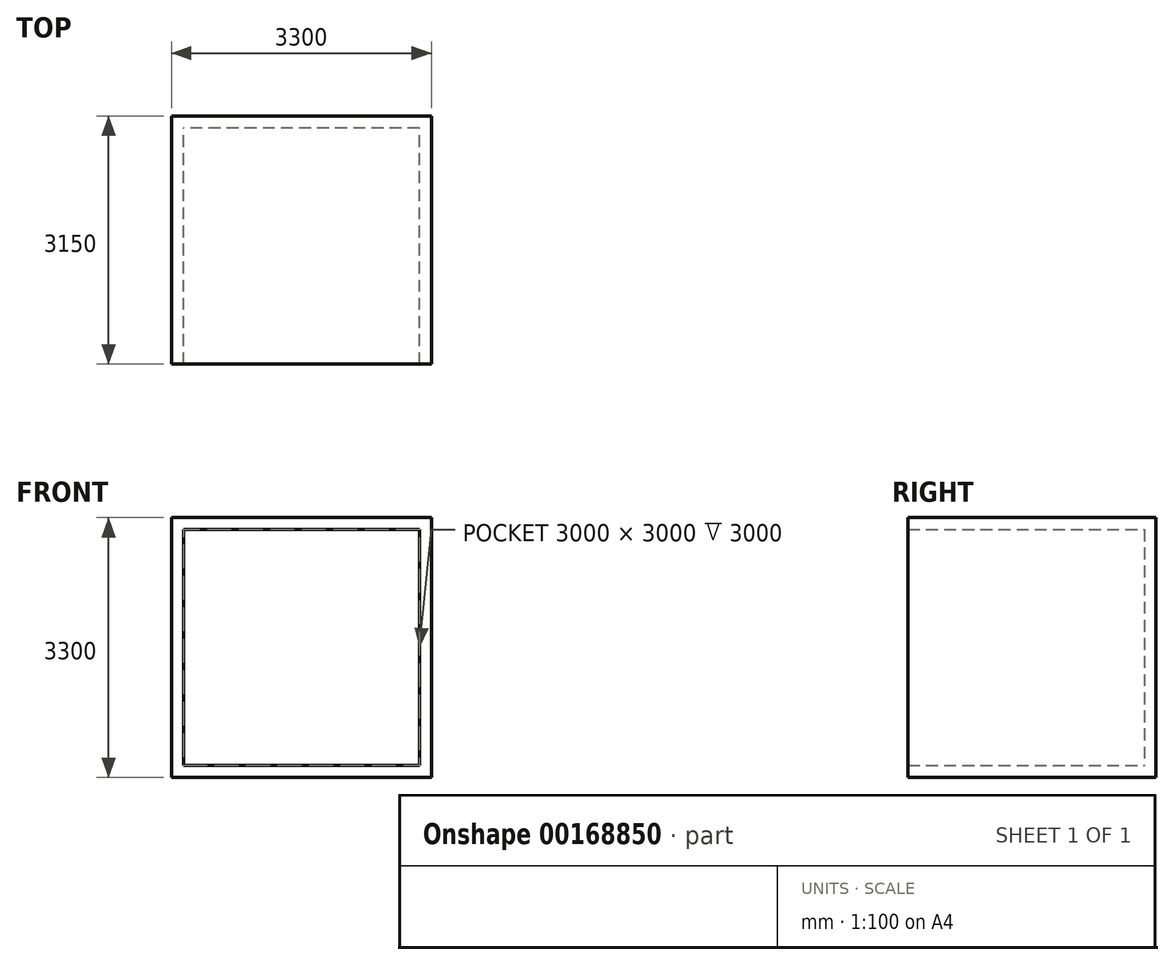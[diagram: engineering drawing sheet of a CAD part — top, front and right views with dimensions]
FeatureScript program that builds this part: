
annotation { "Feature Type Name" : "Feature", "Feature Type Description" : "" }
export const myFeature = defineFeature(function(context is Context, id is Id, definition is map)
    precondition{}
    {
        {
            var Q0;
            Q0=qCreatedBy(makeId("Front.planeOp"),FACE);
            var sketch = newSketch(context, id + "F0", { "sketchPlane" : qUnion([Q0])});
            skLineSegment(sketch, "E0.bottom", {"start": v(1500, 3150) * mm, "end": v(-1500, 3150) * mm});
            skLineSegment(sketch, "E0.top", {"start": v(1500, 150) * mm, "end": v(-1500, 150) * mm});
            skLineSegment(sketch, "E0.left", {"start": v(1500, 3150) * mm, "end": v(1500, 150) * mm});
            skLineSegment(sketch, "E0.right", {"start": v(-1500, 3150) * mm, "end": v(-1500, 150) * mm});
            skPoint(sketch, "E0.middle", {"position": v(0, 1650) * mm});
            skLineSegment(sketch, "E1.0", {"start": v(1650, 3300) * mm, "end": v(-1650, 3300) * mm});
            skLineSegment(sketch, "E1.1", {"start": v(1650, 3300) * mm, "end": v(1650, 0) * mm});
            skLineSegment(sketch, "E1.2", {"start": v(1650, 0) * mm, "end": v(-1650, 0) * mm});
            skLineSegment(sketch, "E1.3", {"start": v(-1650, 3300) * mm, "end": v(-1650, 0) * mm});
            skSolve(sketch);
        }
        {
            var Q0;
            Q0=makeQuery(id+"F0.imprint","IMPRINT",FACE,{"disambiguationData":[TD([[makeQuery(id+"F0.imprint","IMPRINT",EDGE,{"derivedFrom":sQuery(id+"F0.wireOp",EDGE,"E0.bottom")}),1.0]])]});
            extrude(context, id + "F1", {"entities" : qUnion([Q0]), "endBound" : BoundingType.SYMMETRIC, "depth" : 3000 * mm});
        }
        {
            var Q0;
            Q0=makeQuery(id+"F1.opExtrude","CAP_FACE",FACE,{"disambiguationData":[OSD([sQuery(id+"F0.wireOp",EDGE,"E0.bottom"),sQuery(id+"F0.wireOp",EDGE,"E0.top"),sQuery(id+"F0.wireOp",EDGE,"E0.left"),sQuery(id+"F0.wireOp",EDGE,"E0.right")])],"isStart":false});
            shell(context, id + "F2", {"entities" : qUnion([Q0]), "thickness" : 150 * mm, "oppositeDirection" : true});
        }
    });
